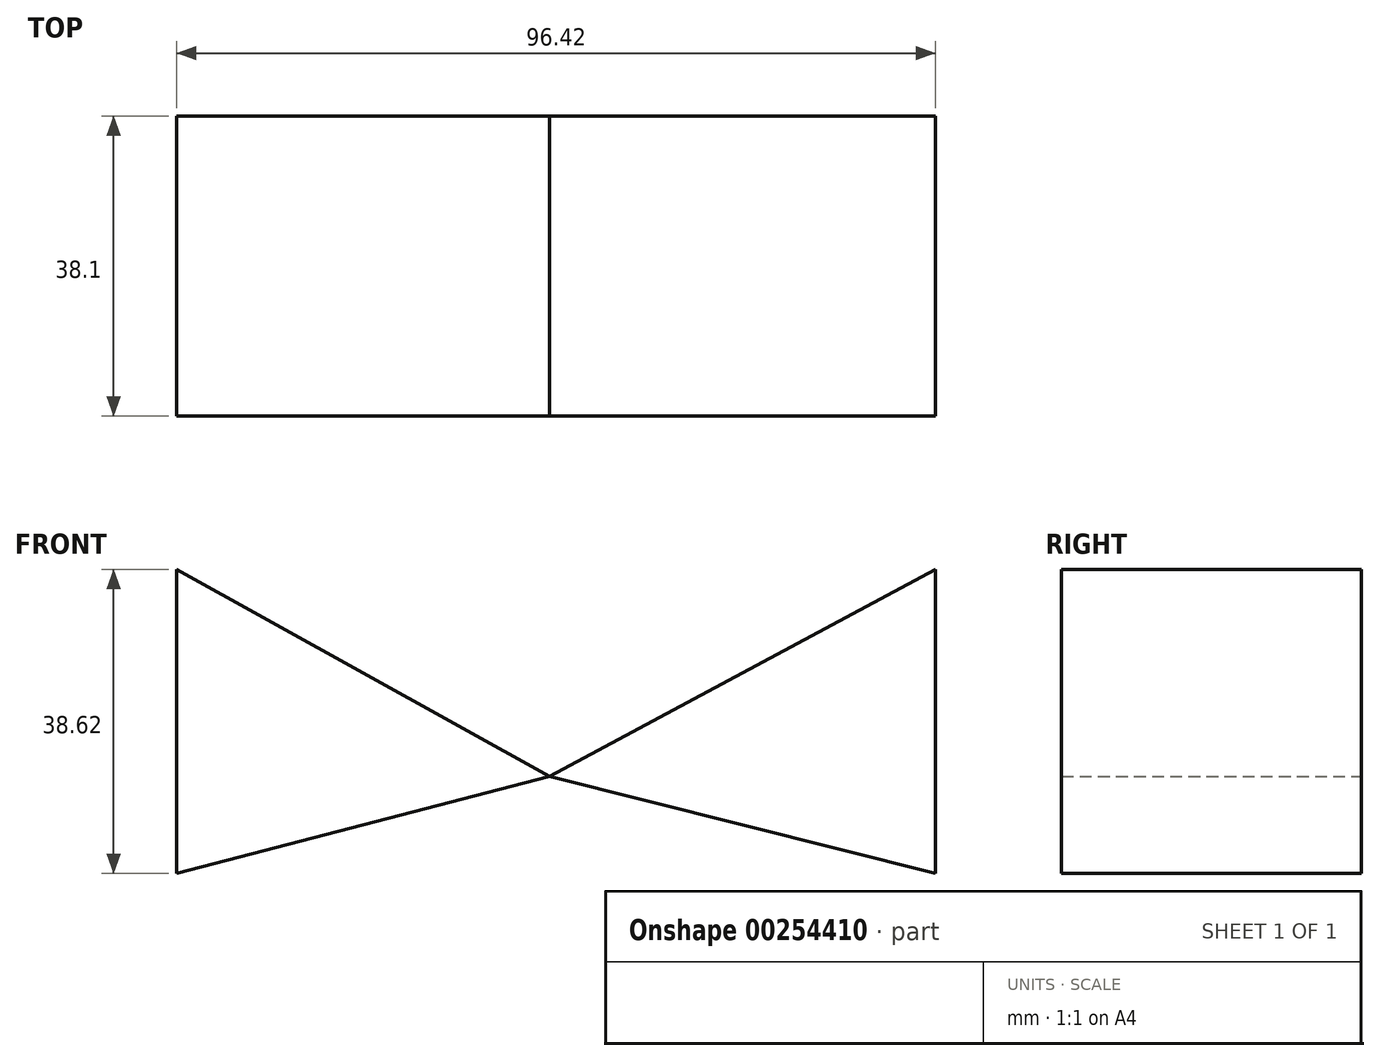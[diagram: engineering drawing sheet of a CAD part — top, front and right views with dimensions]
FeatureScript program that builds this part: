
annotation { "Feature Type Name" : "Feature", "Feature Type Description" : "" }
export const myFeature = defineFeature(function(context is Context, id is Id, definition is map)
    precondition{}
    {
        {
            var Q0;
            Q0=qCreatedBy(makeId("Front.planeOp"),FACE);
            var sketch = newSketch(context, id + "F0", { "sketchPlane" : qUnion([Q0])});
            skLineSegment(sketch, "E0", {"start": v(-47.34, 26.28) * mm, "end": v(0, 0) * mm});
            skLineSegment(sketch, "E1", {"start": v(-47.34, 26.28) * mm, "end": v(-47.34, -12.34) * mm});
            skLineSegment(sketch, "E2", {"start": v(-47.34, -12.34) * mm, "end": v(0, 0) * mm});
            skLineSegment(sketch, "E3", {"start": v(0, 0) * mm, "end": v(49.08, 26.28) * mm});
            skLineSegment(sketch, "E4", {"start": v(49.08, 26.28) * mm, "end": v(49.08, -12.34) * mm});
            skLineSegment(sketch, "E5", {"start": v(49.08, -12.34) * mm, "end": v(0, 0) * mm});
            skSolve(sketch);
        }
        {
            var Q0;
            Q0=makeQuery(id+"F0.imprint","IMPRINT",FACE,{"disambiguationData":[TD([[makeQuery(id+"F0.imprint","IMPRINT",EDGE,{"derivedFrom":sQuery(id+"F0.wireOp",EDGE,"E3")}),-1.0]])]});
            var Q1;
            Q1=makeQuery(id+"F0.imprint","IMPRINT",FACE,{"disambiguationData":[TD([[makeQuery(id+"F0.imprint","IMPRINT",EDGE,{"derivedFrom":sQuery(id+"F0.wireOp",EDGE,"E0")}),-1.0]])]});
            extrude(context, id + "F1", {"entities" : qUnion([Q0, Q1]), "depth" : 38.1 * mm});
        }
    });
